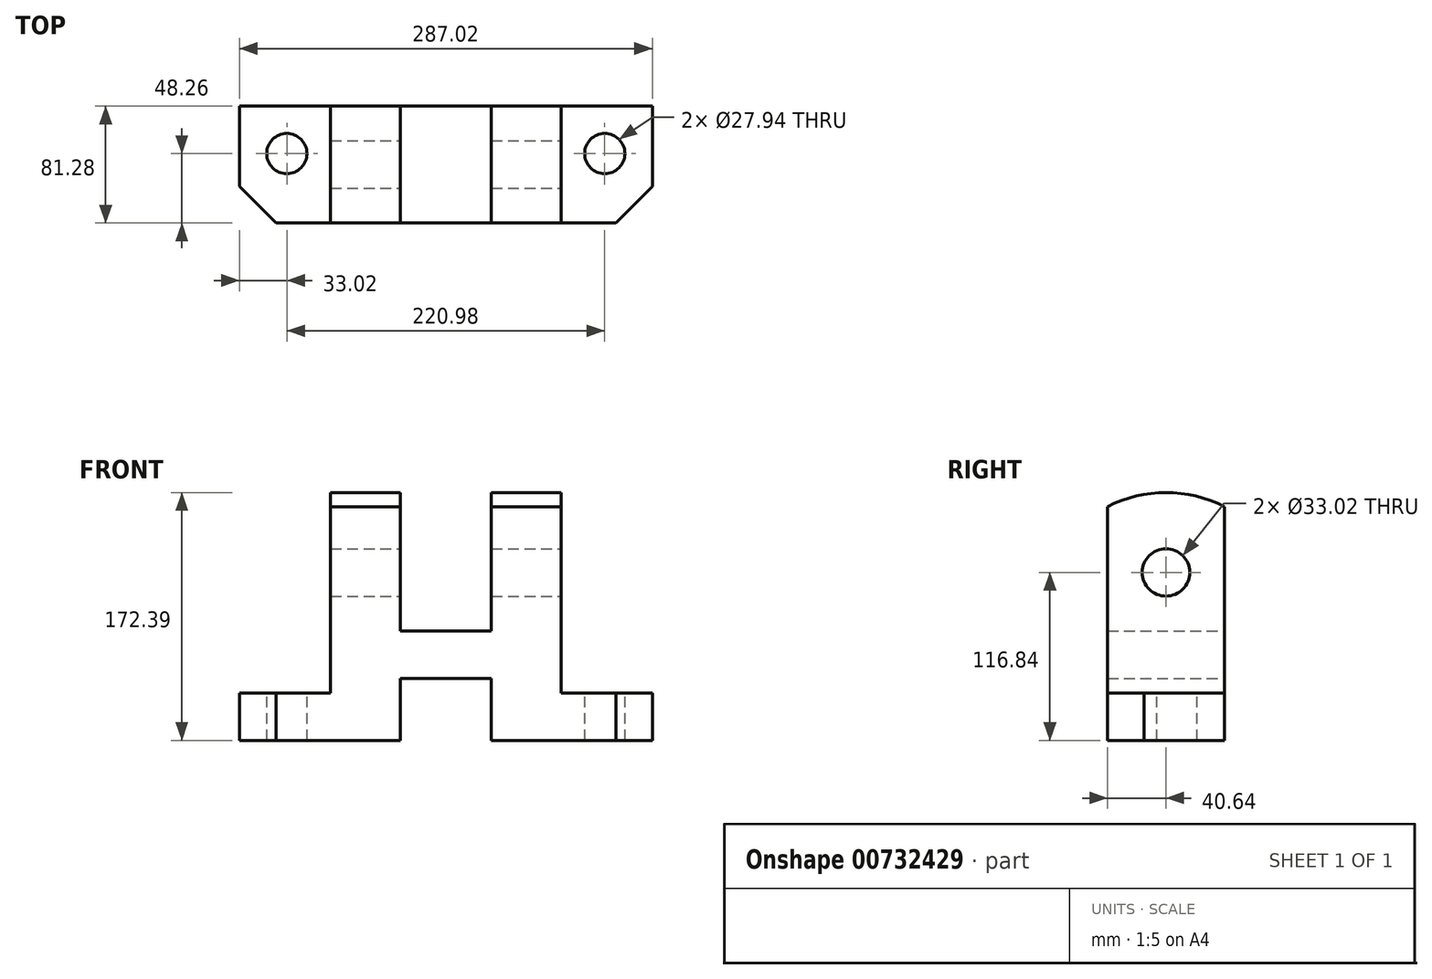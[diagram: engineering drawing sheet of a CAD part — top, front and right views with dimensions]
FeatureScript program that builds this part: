
annotation { "Feature Type Name" : "Feature", "Feature Type Description" : "" }
export const myFeature = defineFeature(function(context is Context, id is Id, definition is map)
    precondition{}
    {
        {
            var Q0;
            Q0=qCreatedBy(makeId("Front.planeOp"),FACE);
            var sketch = newSketch(context, id + "F0", { "sketchPlane" : qUnion([Q0])});
            skLineSegment(sketch, "E0", {"start": v(-31.75, -43.18) * mm, "end": v(-143.51, -43.18) * mm});
            skLineSegment(sketch, "E1", {"start": v(-143.51, -43.18) * mm, "end": v(-143.51, -10.16) * mm});
            skLineSegment(sketch, "E2", {"start": v(-143.51, -10.16) * mm, "end": v(-80.01, -10.16) * mm});
            skLineSegment(sketch, "E3", {"start": v(-80.01, -10.16) * mm, "end": v(-80.01, 139.7) * mm});
            skLineSegment(sketch, "E4", {"start": v(-80.01, 139.7) * mm, "end": v(-31.75, 139.7) * mm});
            skLineSegment(sketch, "E5", {"start": v(-31.75, 139.7) * mm, "end": v(-31.75, 33.02) * mm});
            skLineSegment(sketch, "E6", {"start": v(-31.75, 33.02) * mm, "end": v(31.75, 33.02) * mm});
            skLineSegment(sketch, "E7", {"start": v(31.75, 33.02) * mm, "end": v(31.75, 139.7) * mm});
            skLineSegment(sketch, "E8", {"start": v(31.75, 139.7) * mm, "end": v(80, 139.7) * mm});
            skLineSegment(sketch, "E9", {"start": v(80, 139.7) * mm, "end": v(80.01, -10.16) * mm});
            skLineSegment(sketch, "E10", {"start": v(80.01, -10.16) * mm, "end": v(143.51, -10.16) * mm});
            skLineSegment(sketch, "E11", {"start": v(143.51, -10.16) * mm, "end": v(143.51, -43.18) * mm});
            skLineSegment(sketch, "E12", {"start": v(143.51, -43.18) * mm, "end": v(31.75, -43.18) * mm});
            skLineSegment(sketch, "E13", {"start": v(31.75, -43.18) * mm, "end": v(31.75, 0) * mm});
            skLineSegment(sketch, "E14", {"start": v(31.75, 0) * mm, "end": v(0, 0) * mm});
            skLineSegment(sketch, "E15", {"start": v(0, 0) * mm, "end": v(-31.75, 0) * mm});
            skLineSegment(sketch, "E16", {"start": v(-31.75, 0) * mm, "end": v(-31.75, -43.18) * mm});
            skSolve(sketch);
        }
        {
            var Q0;
            Q0=makeQuery(id+"F0.imprint","IMPRINT",FACE,{"disambiguationData":[TD([[makeQuery(id+"F0.imprint","IMPRINT",EDGE,{"derivedFrom":sQuery(id+"F0.wireOp",EDGE,"E0")}),-1.0]])]});
            extrude(context, id + "F1", {"entities" : qUnion([Q0]), "endBound" : BoundingType.SYMMETRIC, "depth" : 81.28 * mm, "offsetDistance" : 25.4 * mm});
        }
        {
            var Q0;
            Q0=makeQuery(id+"F1.opExtrude","CAP_EDGE",EDGE,{"disambiguationData":[OSD([sQuery(id+"F0.wireOp",EDGE,"E11")])],"isStart":false});
            var Q1;
            Q1=makeQuery(id+"F1.opExtrude","CAP_EDGE",EDGE,{"disambiguationData":[OSD([sQuery(id+"F0.wireOp",EDGE,"E1")])],"isStart":false});
            chamfer(context, id + "F2", {"entities" : qUnion([Q0, Q1]), "width" : 25.4 * mm, "tangentPropagation" : true});
        }
        {
            var Q0;
            Q0=makeQuery(id+"F1.opExtrude","SWEPT_FACE",FACE,{"disambiguationData":[OSD([sQuery(id+"F0.wireOp",EDGE,"E9")])]});
            var sketch = newSketch(context, id + "F3", { "sketchPlane" : qUnion([Q0])});
            skLineSegment(sketch, "E17", {"start": v(-115.52, -43.18) * mm, "end": v(103, -43.18) * mm, "construction": true});
            skLineSegment(sketch, "E18", {"start": v(-115.52, 119.38) * mm, "end": v(103, 119.38) * mm, "construction": true});
            skLineSegment(sketch, "E19", {"start": v(0, 0) * mm, "end": v(0, 145.23) * mm, "construction": true});
            skCircle(sketch, "E20", {"center": v(40.64, 119.38) * mm, "radius": 88.9 * mm, "construction": true});
            skArc(sketch, "E21", {"start": v(40.64, 119.38) * mm, "mid": v(0, 129.21) * mm, "end": v(-40.64, 119.38) * mm});
            skLineSegment(sketch, "E22.0", {"start": v(-40.64, 139.7) * mm, "end": v(-40.64, 119.38) * mm});
            skLineSegment(sketch, "E23.0", {"start": v(-40.64, 139.7) * mm, "end": v(40.64, 139.7) * mm});
            skLineSegment(sketch, "E24.0", {"start": v(40.64, 139.7) * mm, "end": v(40.64, 119.38) * mm});
            skPoint(sketch, "E25.trimOffspring.end.orphan", {"position": v(40.64, -10.16) * mm});
            skPoint(sketch, "E26.orphan", {"position": v(-40.64, -10.16) * mm});
            skCircle(sketch, "E27", {"center": v(0, 73.66) * mm, "radius": 16.51 * mm});
            skSolve(sketch);
        }
        {
            var Q0;
            Q0=makeQuery(id+"F3.imprint","IMPRINT",FACE,{"disambiguationData":[TD([[makeQuery(id+"F3.imprint","IMPRINT",EDGE,{"derivedFrom":sQuery(id+"F3.wireOp",EDGE,"E21")}),-1.0]])]});
            var Q1;
            Q1=makeQuery(id+"F3.imprint","IMPRINT",FACE,{"disambiguationData":[TD([[makeQuery(id+"F3.imprint","IMPRINT",EDGE,{"derivedFrom":sQuery(id+"F3.wireOp",EDGE,"E27")}),1.0]])]});
            extrude(context, id + "F4", {"entities" : qUnion([Q0, Q1]), "operationType" : NewBodyOperationType.REMOVE, "oppositeDirection" : true, "depth" : 160.02 * mm, "offsetDistance" : 25.4 * mm});
        }
        {
            var Q0;
            Q0=makeQuery(id+"F1.opExtrude","SWEPT_FACE",FACE,{"disambiguationData":[OSD([sQuery(id+"F0.wireOp",EDGE,"E10")])]});
            var sketch = newSketch(context, id + "F5", { "sketchPlane" : qUnion([Q0])});
            skCircle(sketch, "E28", {"center": v(110.5, 7.62) * mm, "radius": 13.97 * mm});
            skCircle(sketch, "E29.MirrorC", {"center": v(-110.5, 7.62) * mm, "radius": 13.97 * mm});
            skSolve(sketch);
        }
        {
            var Q0;
            Q0 = qSketchRegion(id + "F5", true);
            extrude(context, id + "F6", {"entities" : qUnion([Q0]), "operationType" : NewBodyOperationType.REMOVE, "oppositeDirection" : true, "depth" : 33.02 * mm, "offsetDistance" : 25.4 * mm});
        }
    });
